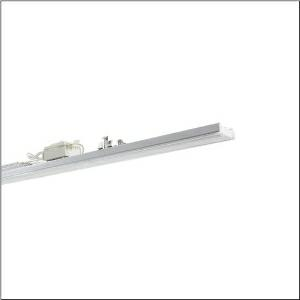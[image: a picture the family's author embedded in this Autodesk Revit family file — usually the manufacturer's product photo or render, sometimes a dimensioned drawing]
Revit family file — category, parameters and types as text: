
# Revit family: licross_r__21_recessed_mo_52tl12dn4axg_5465
name_source: partatom
category: Lighting Fixtures
units: mm (PartAtom-declared; Revit-internal decimal feet)

## family parameters
Cut with Voids When Loaded = No
Host = Face
Light Source = No
Part Type = Normal
Room Calculation Point = No
Round Connector Dimension = Use Diameter
Shared = No

## types (1)
- --- (1 x LED, 10280 lm, 58 W, 4000K)
    Apparent Load = 58 VA
    CIE Flux Codes = 72 92 99 100 100
    Color Rendering = 80
    Color Temperature = 4000K
    Default Elevation = 1800 mm
    Description = Licross® 21 Recessed MO, luminaire insert, of sheet steel, galvanised, coil coated, white, length: 1.500mm, width: 66mm, height: 67mm, LED rated luminous flux: 10.280lm, light colour: 840, control gear: DALI 2, with plug, 5-pole, with phase selection, mains connection: 220..240V, AC, 50/60Hz, rated input power: 58W, halogen-free wiring, primary optical cover: cover, of PMMA, light emission: direct distribution, primary light characteristic: symmetric, protection rating (complete): IP40, insulation class (complete): insulation class I (protective earthing), certification: CE, ENEC, VDE, UKCA, protection symbol: D if used in an environment without relevant dust loads with corresponding accessories, impact resistance: IK06, permissible ambient temperature for indoor applications: -25..+35°C, corresponds to IFS (International Featured Standards) requirements for safety and quality in the food industry, reducing of maximum allowable ambient temperature of 5°C with ceiling mounting, LABS conformity tested according to VDMA 24364:2018-05, packaging unit: 1 piece
    Height = 58 mm
    Lamp = 1 x LED
    Lamp Light Flux = 10280 lm
    Lamp Power = 58 W
    Lamp count = 1
    Length = 1500 mm
    Luminous efficacy = 177 lm/W
    Manufacturer = Siteco
    ModVariant = No
    Model = 52TL12DN4AXG
    Mounting Place = Ceiling
    Mounting Type = Pendant
    Number of Poles = 1
    OnlyDefault = Yes
    Power Factor = 1
    Product Name = Licross® 21 Recessed MO
    Product group = luminaire insert
    ProductGroupID = 902
    Protection Class = Protection class I
    Protection Degree = IP 40
    RLX_Detail_Level = 1
    RLX_Emergency_Light_Flux = 0 lm
    RLX_Emergency_Type = 0
    RLX_Emergency_Type_DB = No
    RlxData = <blob elided: 24629 chars, md5=9e54fa07>
    Socket = socket
    Standby Power = 0 W
    System Light Flux = 10280 lm
    System Power = 58 W
    Type Comments = factory setting: luminous flux: 100 % | dim-lin: 254 | 390 mA
    Type Image = l_1296930.jpg
    URL = http://relux.com
    VarID = @adj_126328
    Voltage = 0 V
    Weight = 0.00 kg
    Width = 66 mm

## geometry (parser evidence)
native form markers: Blend x4, Sweep x11
no freeform markers — native parametric forms only
